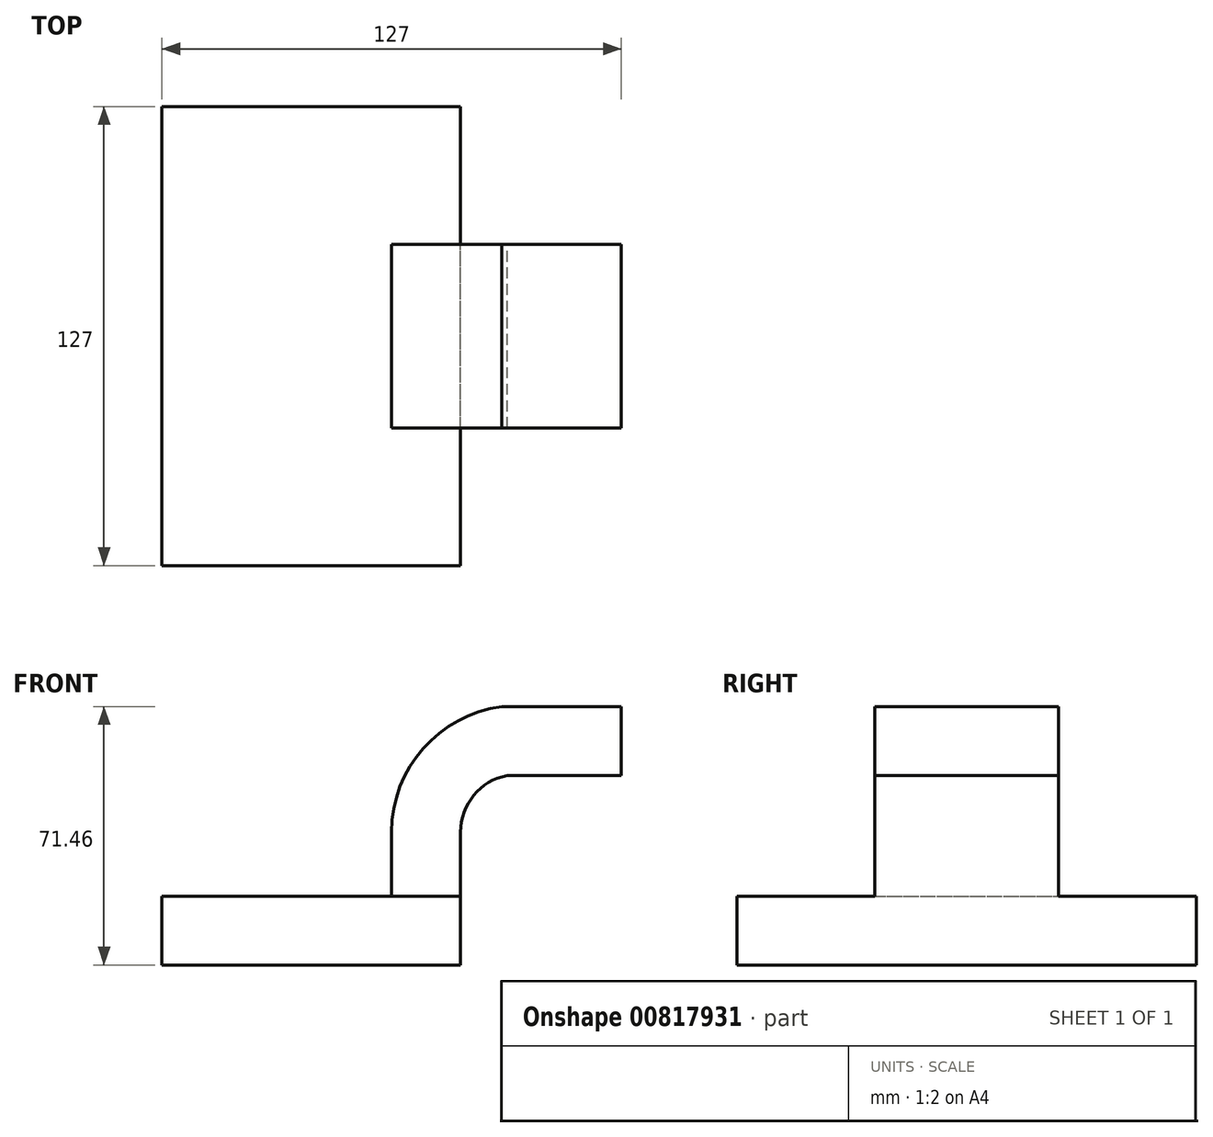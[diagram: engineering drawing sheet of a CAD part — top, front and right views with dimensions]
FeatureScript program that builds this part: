
annotation { "Feature Type Name" : "Feature", "Feature Type Description" : "" }
export const myFeature = defineFeature(function(context is Context, id is Id, definition is map)
    precondition{}
    {
        {
            var Q0;
            Q0=qCreatedBy(makeId("Front.planeOp"),FACE);
            var sketch = newSketch(context, id + "F0", { "sketchPlane" : qUnion([Q0])});
            skLineSegment(sketch, "E0.bottom", {"start": v(41.28, -9.52) * mm, "end": v(-41.27, -9.53) * mm});
            skLineSegment(sketch, "E0.top", {"start": v(41.27, 9.53) * mm, "end": v(-41.28, 9.53) * mm});
            skLineSegment(sketch, "E0.left", {"start": v(41.28, -9.52) * mm, "end": v(41.28, 9.53) * mm});
            skLineSegment(sketch, "E0.right", {"start": v(-41.27, -9.53) * mm, "end": v(-41.28, 9.52) * mm});
            skPoint(sketch, "E0.middle", {"position": v(0, 0) * mm});
            skLineSegment(sketch, "E1.bottom", {"start": v(111.12, 38.1) * mm, "end": v(60.32, 38.1) * mm});
            skLineSegment(sketch, "E1.top", {"start": v(111.12, 66.68) * mm, "end": v(60.32, 66.68) * mm});
            skLineSegment(sketch, "E1.left", {"start": v(111.12, 38.1) * mm, "end": v(111.12, 66.68) * mm});
            skLineSegment(sketch, "E1.right", {"start": v(60.32, 38.1) * mm, "end": v(60.32, 66.68) * mm});
            skPoint(sketch, "E1.middle", {"position": v(85.72, 52.39) * mm});
            skLineSegment(sketch, "E2", {"start": v(41.27, 9.53) * mm, "end": v(41.27, 27.29) * mm});
            skArc(sketch, "E3", {"start": v(41.27, 27.29) * mm, "mid": v(44.91, 37.4) * mm, "end": v(54.15, 42.88) * mm});
            skLineSegment(sketch, "E4", {"start": v(54.15, 42.88) * mm, "end": v(85.73, 42.88) * mm});
            skLineSegment(sketch, "E5.0", {"start": v(52.7, 61.93) * mm, "end": v(85.73, 61.93) * mm});
            skArc(sketch, "E5.1", {"start": v(22.23, 27.29) * mm, "mid": v(30.93, 50.35) * mm, "end": v(52.7, 61.93) * mm});
            skLineSegment(sketch, "E5.2", {"start": v(22.22, 9.53) * mm, "end": v(22.22, 27.29) * mm});
            skLineSegment(sketch, "E6", {"start": v(85.73, 61.93) * mm, "end": v(85.73, 42.88) * mm});
            skFitSpline(sketch, "E7", {"points": [v(52.7, 61.93) * mm, v(-41.28, 9.52) * mm], "startDerivative": vector(-110.68, -14.09) * mm, "endDerivative": vector(-58.52, -94.66) * mm});
            skLineSegment(sketch, "E8", {"start": v(85.72, 66.68) * mm, "end": v(85.72, 38.1) * mm});
            skSolve(sketch);
        }
        {
            var Q0;
            Q0=makeQuery(id+"F0.imprint","IMPRINT",FACE,{"disambiguationData":[TD([[makeQuery(id+"F0.imprint","IMPRINT",EDGE,{"derivedFrom":sQuery(id+"F0.wireOp",EDGE,"E0.bottom")}),-1.0]])]});
            extrude(context, id + "F1", {"entities" : qUnion([Q0]), "endBound" : BoundingType.SYMMETRIC, "depth" : 127 * mm, "offsetDistance" : 25.4 * mm});
        }
        {
            var Q0;
            {var subQ1=sQuery(id+"F0.wireOp",EDGE,"E2");Q0=makeQuery(id+"F0.imprint","IMPRINT",FACE,{"disambiguationData":[TD([[makeQuery(id+"F0.imprint","IMPRINT",EDGE,{"derivedFrom":subQ1}),1.0]])]});}
            var Q1;
            {var subQ5=sQuery(id+"F0.wireOp",EDGE,"E6");Q1=makeQuery(id+"F0.imprint","IMPRINT",FACE,{"disambiguationData":[TD([[makeQuery(id+"F0.imprint","IMPRINT",EDGE,{"derivedFrom":subQ5}),-1.0]])]});}
            extrude(context, id + "F2", {"entities" : qUnion([Q0, Q1]), "operationType" : NewBodyOperationType.ADD, "endBound" : BoundingType.SYMMETRIC, "depth" : 50.8 * mm, "offsetDistance" : 25.4 * mm});
        }
        {
            var Q0;
            Q0=makeQuery(id+"F0.imprint","IMPRINT",FACE,{"disambiguationData":[TD([[makeQuery(id+"F0.imprint","IMPRINT",EDGE,{"derivedFrom":sQuery(id+"F0.wireOp",EDGE,"E5.1")}),1.0]])]});
            extrude(context, id + "F3", {"entities" : qUnion([Q0]), "operationType" : NewBodyOperationType.ADD, "endBound" : BoundingType.SYMMETRIC, "depth" : 15.88 * mm, "offsetDistance" : 25.4 * mm});
        }
    });
